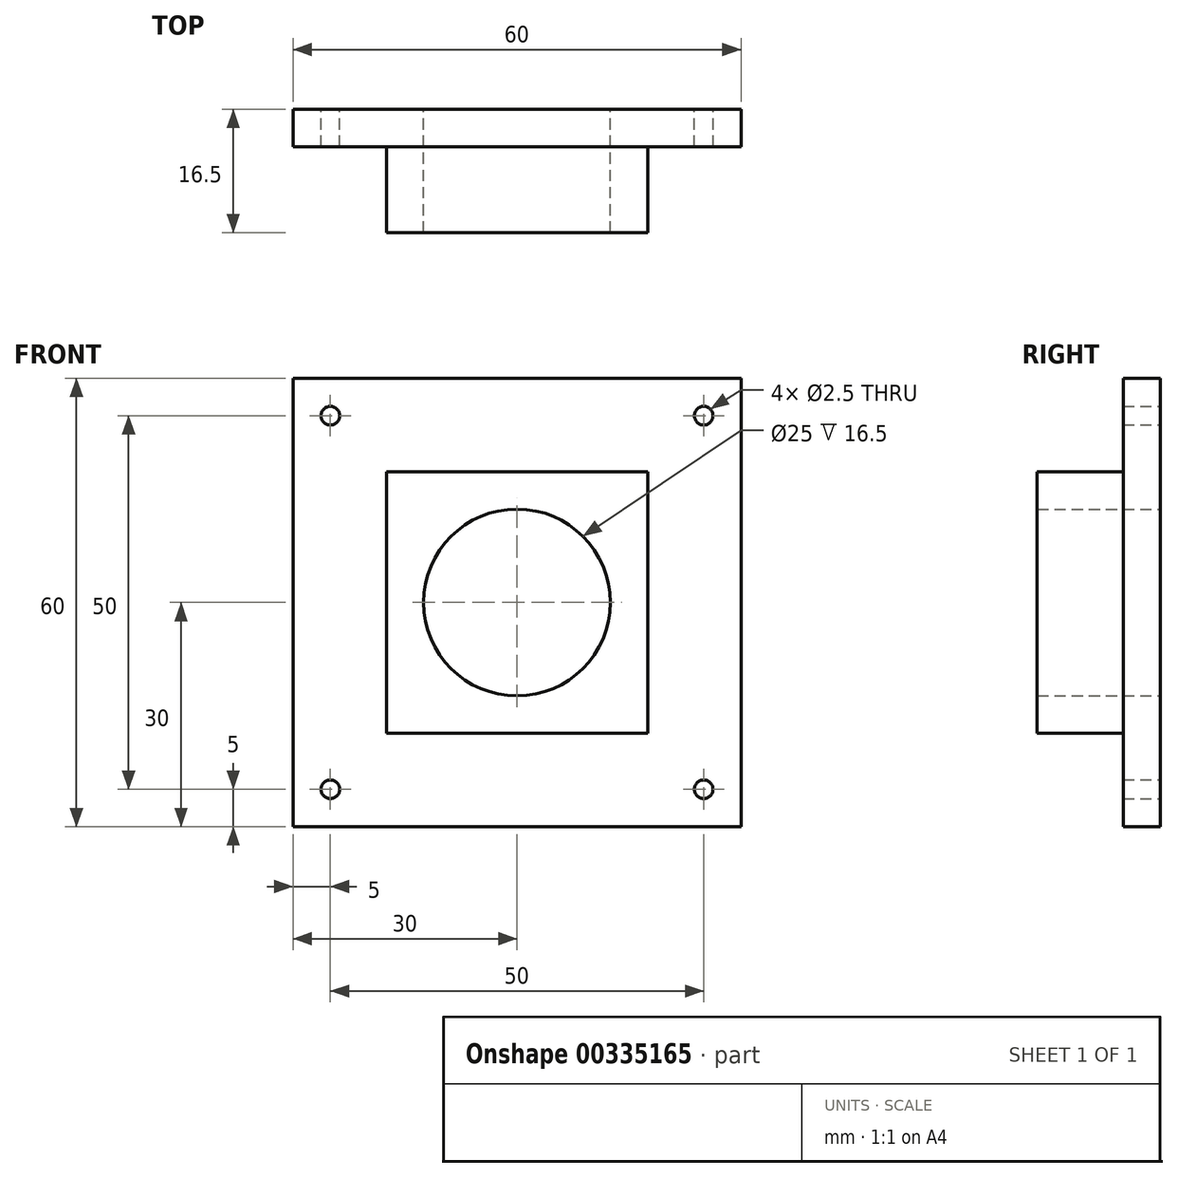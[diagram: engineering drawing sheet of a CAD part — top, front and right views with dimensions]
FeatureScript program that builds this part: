
annotation { "Feature Type Name" : "Feature", "Feature Type Description" : "" }
export const myFeature = defineFeature(function(context is Context, id is Id, definition is map)
    precondition{}
    {
        {
            var Q0;
            Q0=qCreatedBy(makeId("Front.planeOp"),FACE);
            var sketch = newSketch(context, id + "F0", { "sketchPlane" : qUnion([Q0])});
            skLineSegment(sketch, "E0.bottom", {"start": v(20.25, -20.25) * mm, "end": v(-20.25, -20.25) * mm});
            skLineSegment(sketch, "E0.top", {"start": v(20.25, 20.25) * mm, "end": v(-20.25, 20.25) * mm});
            skLineSegment(sketch, "E0.left", {"start": v(20.25, -20.25) * mm, "end": v(20.25, 20.25) * mm});
            skLineSegment(sketch, "E0.right", {"start": v(-20.25, -20.25) * mm, "end": v(-20.25, 20.25) * mm});
            skPoint(sketch, "E0.middle", {"position": v(0, 0) * mm});
            skLineSegment(sketch, "E1.bottom", {"start": v(30, -30) * mm, "end": v(-30, -30) * mm});
            skLineSegment(sketch, "E1.top", {"start": v(30, 30) * mm, "end": v(-30, 30) * mm});
            skLineSegment(sketch, "E1.left", {"start": v(30, -30) * mm, "end": v(30, 30) * mm});
            skLineSegment(sketch, "E1.right", {"start": v(-30, -30) * mm, "end": v(-30, 30) * mm});
            skCircle(sketch, "E2", {"center": v(0, 0) * mm, "radius": 12.5 * mm});
            skCircle(sketch, "E3", {"center": v(-25, 25) * mm, "radius": 1.25 * mm});
            skCircle(sketch, "E4", {"center": v(-25, -25) * mm, "radius": 1.25 * mm});
            skCircle(sketch, "E5", {"center": v(25, 25) * mm, "radius": 1.25 * mm});
            skCircle(sketch, "E6", {"center": v(25, -25) * mm, "radius": 1.25 * mm});
            skSolve(sketch);
        }
        {
            var Q0;
            Q0=makeQuery(id+"F0.imprint","IMPRINT",FACE,{"disambiguationData":[TD([[makeQuery(id+"F0.imprint","IMPRINT",EDGE,{"derivedFrom":sQuery(id+"F0.wireOp",EDGE,"E0.bottom")}),1.0]])]});
            var Q1;
            Q1=makeQuery(id+"F0.imprint","IMPRINT",FACE,{"disambiguationData":[TD([[makeQuery(id+"F0.imprint","IMPRINT",EDGE,{"derivedFrom":sQuery(id+"F0.wireOp",EDGE,"E0.bottom")}),-1.0]])]});
            extrude(context, id + "F1", {"entities" : qUnion([Q0, Q1]), "depth" : 16.5 * mm});
        }
        {
            var Q0;
            Q0=makeQuery(id+"F1.opExtrude","CAP_FACE",FACE,{"disambiguationData":[OSD([sQuery(id+"F0.wireOp",EDGE,"E1.bottom"),sQuery(id+"F0.wireOp",EDGE,"E1.top"),sQuery(id+"F0.wireOp",EDGE,"E1.left"),sQuery(id+"F0.wireOp",EDGE,"E1.right"),sQuery(id+"F0.wireOp",EDGE,"E2"),sQuery(id+"F0.wireOp",EDGE,"E3"),sQuery(id+"F0.wireOp",EDGE,"E4"),sQuery(id+"F0.wireOp",EDGE,"E5"),sQuery(id+"F0.wireOp",EDGE,"E6")])],"isStart":false});
            var sketch = newSketch(context, id + "F2", { "sketchPlane" : qUnion([Q0])});
            skLineSegment(sketch, "E7.bottom", {"start": v(17.5, -17.5) * mm, "end": v(-17.5, -17.5) * mm});
            skLineSegment(sketch, "E7.top", {"start": v(17.5, 17.5) * mm, "end": v(-17.5, 17.5) * mm});
            skLineSegment(sketch, "E7.left", {"start": v(17.5, -17.5) * mm, "end": v(17.5, 17.5) * mm});
            skLineSegment(sketch, "E7.right", {"start": v(-17.5, -17.5) * mm, "end": v(-17.5, 17.5) * mm});
            skPoint(sketch, "E7.middle", {"position": v(0, 0) * mm});
            skSolve(sketch);
        }
        {
            var Q0;
            Q0=makeQuery(id+"F2.imprint","IMPRINT",FACE,{"disambiguationData":[TD([[makeQuery(id+"F2.imprint","IMPRINT",EDGE,{"derivedFrom":sQuery(id+"F2.wireOp",EDGE,"E7.bottom")}),1.0]])]});
            extrude(context, id + "F3", {"entities" : qUnion([Q0]), "operationType" : NewBodyOperationType.REMOVE, "oppositeDirection" : true, "depth" : 11.5 * mm});
        }
    });
